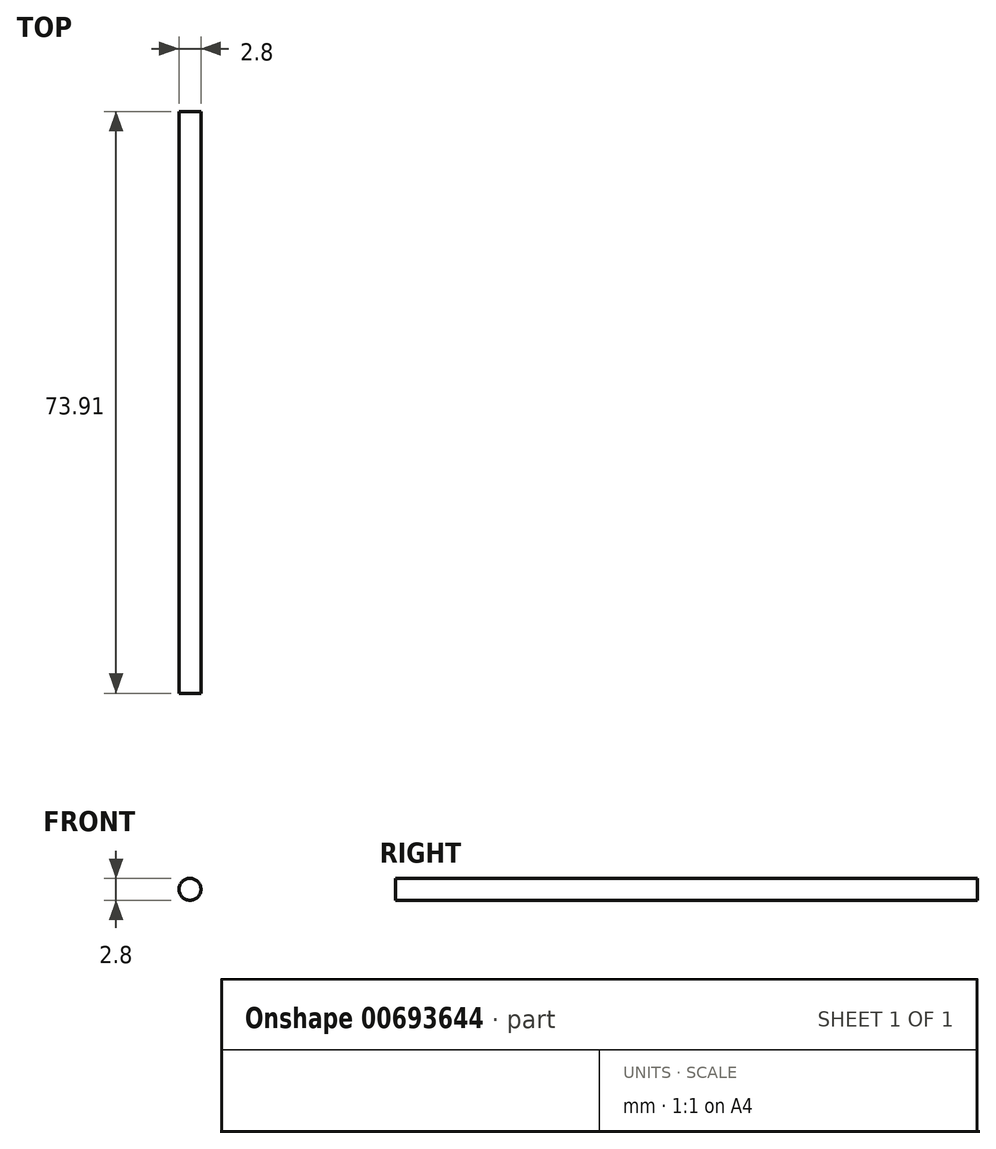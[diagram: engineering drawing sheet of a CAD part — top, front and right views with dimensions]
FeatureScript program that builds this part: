
annotation { "Feature Type Name" : "Feature", "Feature Type Description" : "" }
export const myFeature = defineFeature(function(context is Context, id is Id, definition is map)
    precondition{}
    {
        {
            var Q0;
            Q0=qCreatedBy(makeId("Front.planeOp"),FACE);
            var sketch = newSketch(context, id + "F0", { "sketchPlane" : qUnion([Q0])});
            skCircle(sketch, "E0", {"center": v(0, 0) * mm, "radius": 1.4 * mm});
            skSolve(sketch);
        }
        {
            var Q0;
            Q0 = qSketchRegion(id + "F0", true);
            extrude(context, id + "F1", {"entities" : qUnion([Q0]), "depth" : 73.9 * mm, "offsetDistance" : 25.4 * mm});
        }
    });
